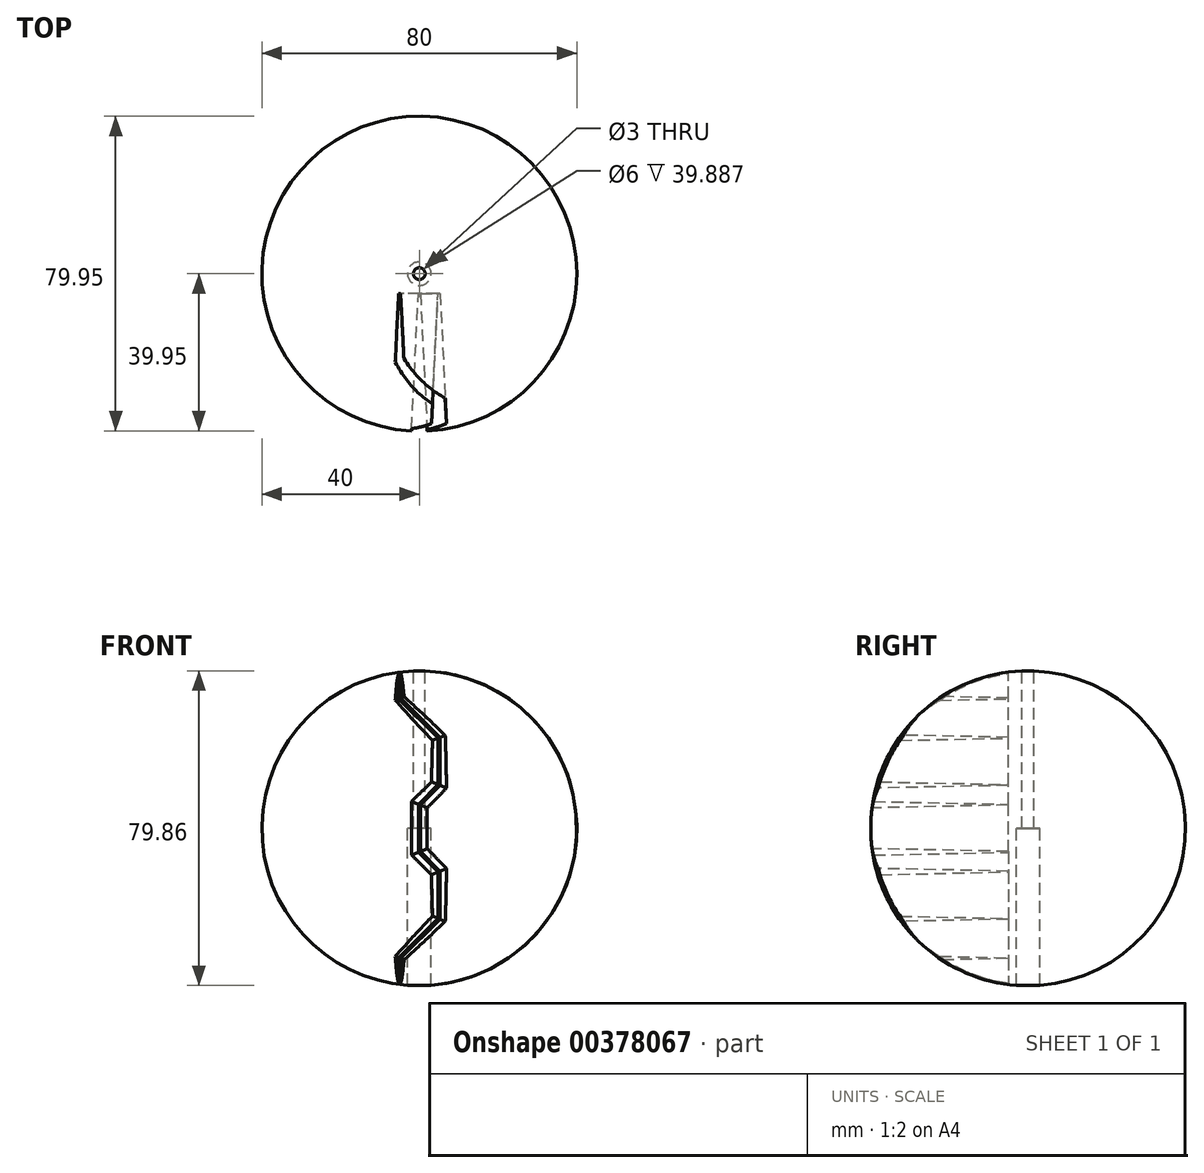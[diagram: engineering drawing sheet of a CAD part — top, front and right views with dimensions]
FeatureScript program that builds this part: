
annotation { "Feature Type Name" : "Feature", "Feature Type Description" : "" }
export const myFeature = defineFeature(function(context is Context, id is Id, definition is map)
    precondition{}
    {
        {
            var Q0;
            Q0=qCreatedBy(makeId("Front.planeOp"),FACE);
            var sketch = newSketch(context, id + "F0", { "sketchPlane" : qUnion([Q0])});
            skArc(sketch, "E0", {"start": v(40, 0) * mm, "mid": v(28.28, 28.28) * mm, "end": v(0, 40) * mm});
            skLineSegment(sketch, "E1", {"start": v(0, 0) * mm, "end": v(0, 40) * mm});
            skLineSegment(sketch, "E2", {"start": v(0, 40) * mm, "end": v(0, 116.26) * mm, "construction": true});
            skLineSegment(sketch, "E3", {"start": v(0, 0) * mm, "end": v(40, 0) * mm});
            skPoint(sketch, "E4.orphan", {"position": v(0, -40) * mm});
            skSolve(sketch);
        }
        {
            var Q0;
            Q0=makeQuery(id+"F0.imprint","IMPRINT",FACE,{"disambiguationData":[TD([[makeQuery(id+"F0.imprint","IMPRINT",EDGE,{"derivedFrom":sQuery(id+"F0.wireOp",EDGE,"E0")}),1.0]])]});
            var Q1;
            Q1=sQuery(id+"F0.wireOp",EDGE,"E2");
            revolve(context, id + "F1", {"entities" : qUnion([Q0]), "axis" : qUnion([Q1]), "revolveType" : RevolveType.FULL});
        }
        {
            var Q0;
            Q0=qCreatedBy(makeId("Front.planeOp"),FACE);
            cPlane(context, id + "F2", {"entities" : qUnion([Q0]), "cplaneType" : CPlaneType.OFFSET, "offset" : 5 * mm, "width" : 150 * mm, "height" : 150 * mm});
        }
        {
            var Q0;
            Q0=qCreatedBy(id+"F2.planeOp",FACE);
            var sketch = newSketch(context, id + "F3", { "sketchPlane" : qUnion([Q0])});
            skLineSegment(sketch, "E5", {"start": v(0, 0) * mm, "end": v(0, 6) * mm});
            skLineSegment(sketch, "E6", {"start": v(0, 6) * mm, "end": v(5, 11) * mm});
            skLineSegment(sketch, "E7", {"start": v(5, 11) * mm, "end": v(5, 23) * mm});
            skLineSegment(sketch, "E8", {"start": v(5, 23) * mm, "end": v(-5, 33) * mm});
            skLineSegment(sketch, "E9", {"start": v(-5, 33) * mm, "end": v(-5, 43.72) * mm});
            skSolve(sketch);
        }
        {
            var Q0;
            Q0=qCreatedBy(makeId("Top.planeOp"),FACE);
            var sketch = newSketch(context, id + "F4", { "sketchPlane" : qUnion([Q0])});
            skLineSegment(sketch, "E10.bottom", {"start": v(-2.75, -54.94) * mm, "end": v(2.75, -54.94) * mm});
            skLineSegment(sketch, "E10.top", {"start": v(-0.25, -5) * mm, "end": v(0.25, -5) * mm});
            skLineSegment(sketch, "E10.left", {"start": v(-2.75, -54.94) * mm, "end": v(-0.25, -5) * mm});
            skLineSegment(sketch, "E10.right", {"start": v(2.75, -54.94) * mm, "end": v(0.25, -5) * mm});
            skLineSegment(sketch, "E11", {"start": v(0, 0) * mm, "end": v(0, 26.22) * mm, "construction": true});
            skSolve(sketch);
        }
        {
            var Q0;
            Q0=makeQuery(id+"F4.imprint","IMPRINT",FACE,{"disambiguationData":[TD([[makeQuery(id+"F4.imprint","IMPRINT",EDGE,{"derivedFrom":sQuery(id+"F4.wireOp",EDGE,"E10.bottom")}),1.0]])]});
            var Q1;
            Q1=sQuery(id+"F3.wireOp",EDGE,"E5");
            var Q2;
            Q2=sQuery(id+"F3.wireOp",EDGE,"E6");
            var Q3;
            Q3=sQuery(id+"F3.wireOp",EDGE,"E7");
            var Q4;
            Q4=sQuery(id+"F3.wireOp",EDGE,"E8");
            var Q5;
            Q5=sQuery(id+"F3.wireOp",EDGE,"E9");
            sweep(context, id + "F5", {"operationType" : NewBodyOperationType.REMOVE, "profiles" : qUnion([Q0]), "path" : qUnion([Q1, Q2, Q3, Q4, Q5])});
        }
        {
            var Q0;
            Q0=makeQuery(id+"F1.opRevolve","SWEPT_BODY",BODY,{"disambiguationData":[OSD([sQuery(id+"F0.wireOp",EDGE,"E0"),sQuery(id+"F0.wireOp",EDGE,"E1"),sQuery(id+"F0.wireOp",EDGE,"E3")])]});
            var Q1;
            Q1=qCreatedBy(makeId("Top.planeOp"),FACE);
            mirror(context, id + "F6", {"operationType" : NewBodyOperationType.ADD, "entities" : qUnion([Q0]), "mirrorPlane" : qUnion([Q1])});
        }
        {
            var Q0;
            Q0=qCreatedBy(makeId("Front.planeOp"),FACE);
            var sketch = newSketch(context, id + "F7", { "sketchPlane" : qUnion([Q0])});
            skLineSegment(sketch, "E12", {"start": v(1.5, 100) * mm, "end": v(1.5, 0) * mm});
            skLineSegment(sketch, "E13", {"start": v(1.5, 0) * mm, "end": v(3, 0) * mm});
            skLineSegment(sketch, "E14", {"start": v(3, 0) * mm, "end": v(3, -100) * mm});
            skLineSegment(sketch, "E15", {"start": v(3, -100) * mm, "end": v(0, -100) * mm});
            skLineSegment(sketch, "E16", {"start": v(0, -100) * mm, "end": v(0, 100) * mm});
            skLineSegment(sketch, "E17", {"start": v(0, 100) * mm, "end": v(1.5, 100) * mm});
            skSolve(sketch);
        }
        {
            var Q0;
            Q0=makeQuery(id+"F7.imprint","IMPRINT",FACE,{"disambiguationData":[TD([[makeQuery(id+"F7.imprint","IMPRINT",EDGE,{"derivedFrom":sQuery(id+"F7.wireOp",EDGE,"E12")}),-1.0]])]});
            var Q1;
            Q1=sQuery(id+"F0.wireOp",EDGE,"E2");
            revolve(context, id + "F8", {"operationType" : NewBodyOperationType.REMOVE, "entities" : qUnion([Q0]), "axis" : qUnion([Q1]), "revolveType" : RevolveType.FULL, "oppositeDirection" : true});
        }
    });
